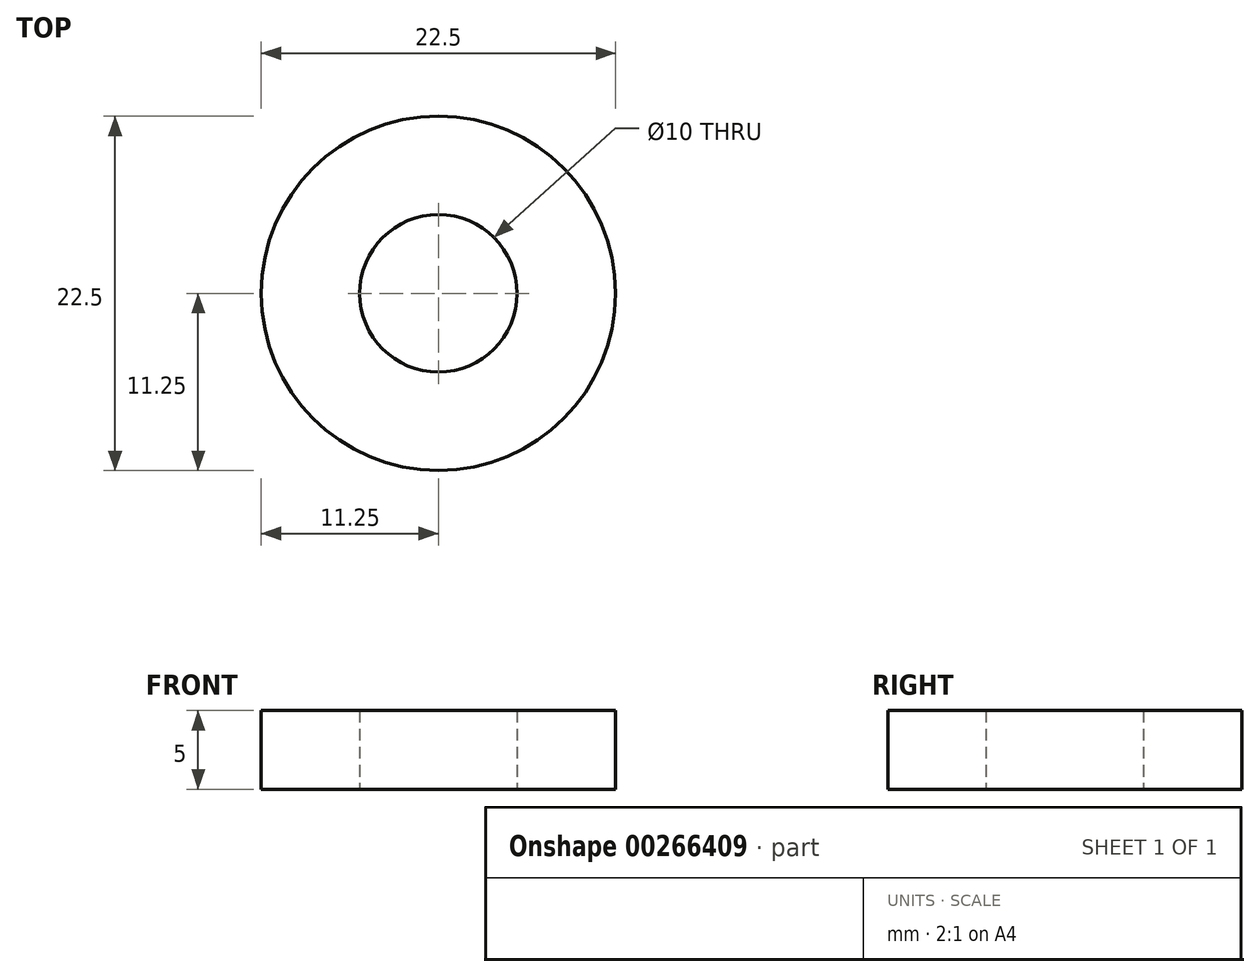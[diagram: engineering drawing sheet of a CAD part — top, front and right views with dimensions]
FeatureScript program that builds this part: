
annotation { "Feature Type Name" : "Feature", "Feature Type Description" : "" }
export const myFeature = defineFeature(function(context is Context, id is Id, definition is map)
    precondition{}
    {
        {
            var Q0;
            Q0=qCreatedBy(makeId("Top.planeOp"),FACE);
            var sketch = newSketch(context, id + "F0", { "sketchPlane" : qUnion([Q0])});
            skCircle(sketch, "E0", {"center": v(0, 0) * mm, "radius": 11.25 * mm});
            skCircle(sketch, "E1", {"center": v(0, 0) * mm, "radius": 5 * mm});
            skSolve(sketch);
        }
        {
            var Q0;
            Q0=makeQuery(id+"F0.imprint","IMPRINT",FACE,{"disambiguationData":[TD([[makeQuery(id+"F0.imprint","IMPRINT",EDGE,{"derivedFrom":sQuery(id+"F0.wireOp",EDGE,"E0")}),1.0]])]});
            extrude(context, id + "F1", {"entities" : qUnion([Q0]), "depth" : 2.5 * mm, "hasSecondDirection" : true, "secondDirectionOppositeDirection" : true, "secondDirectionDepth" : 2.5 * mm});
        }
    });
